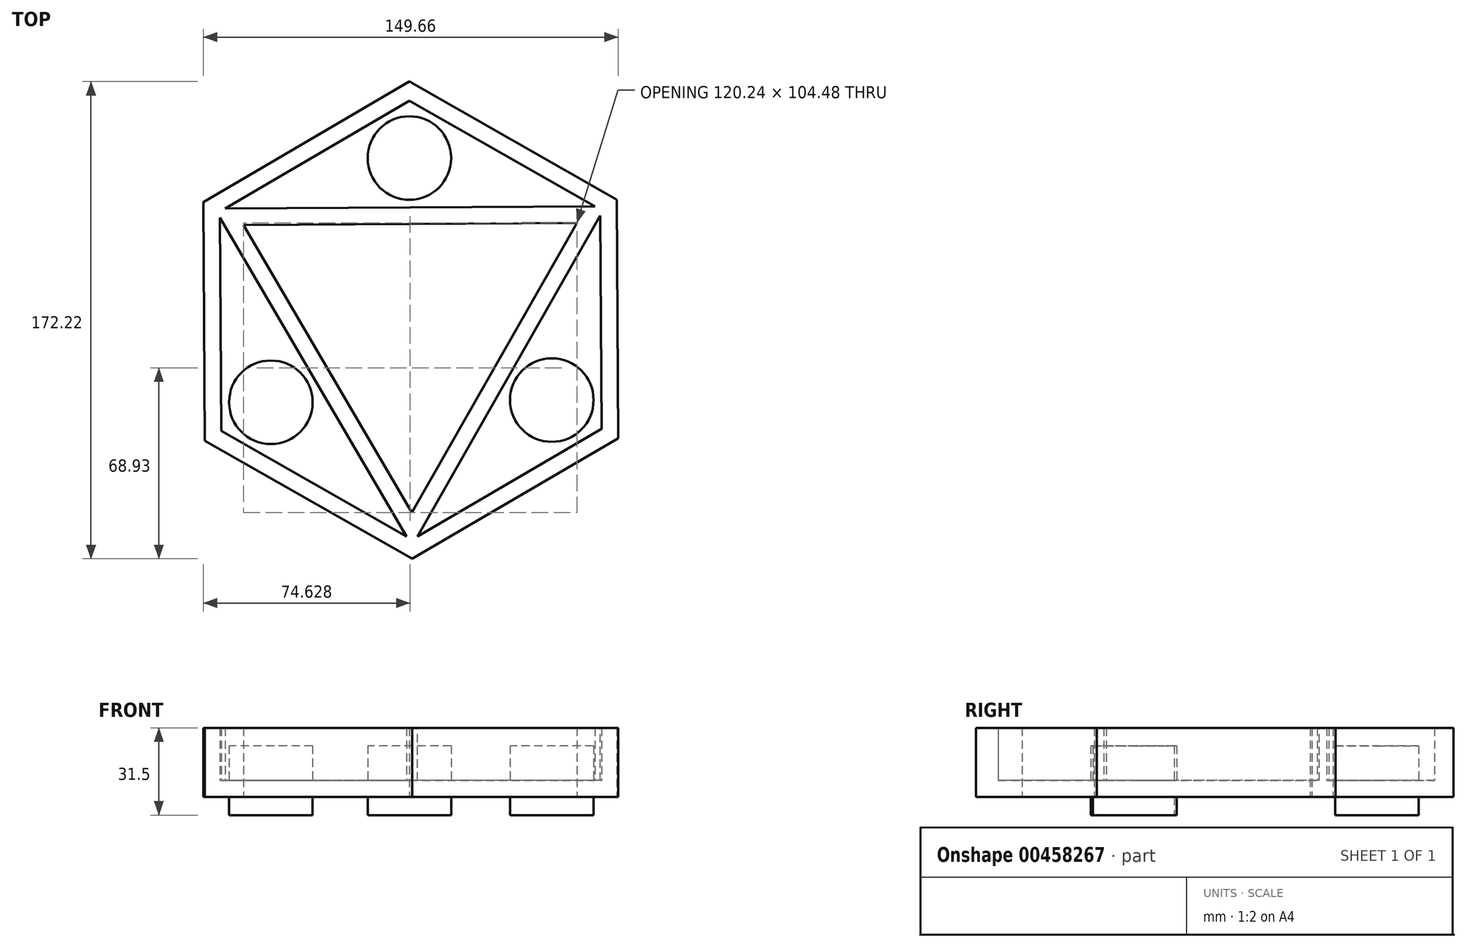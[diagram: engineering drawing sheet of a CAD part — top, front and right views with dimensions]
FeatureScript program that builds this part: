
annotation { "Feature Type Name" : "Feature", "Feature Type Description" : "" }
export const myFeature = defineFeature(function(context is Context, id is Id, definition is map)
    precondition{}
    {
        {
            var Q0;
            Q0=qCreatedBy(makeId("Top.planeOp"),FACE);
            var sketch = newSketch(context, id + "F0", { "sketchPlane" : qUnion([Q0])});
            skLineSegment(sketch, "E0.0", {"start": v(-0.5, 86.11) * mm, "end": v(74.32, 43.5) * mm});
            skLineSegment(sketch, "E0.1", {"start": v(74.32, 43.5) * mm, "end": v(74.83, -42.62) * mm});
            skLineSegment(sketch, "E0.2", {"start": v(74.83, -42.62) * mm, "end": v(0.5, -86.11) * mm});
            skLineSegment(sketch, "E0.3", {"start": v(0.5, -86.11) * mm, "end": v(-74.32, -43.5) * mm});
            skLineSegment(sketch, "E0.4", {"start": v(-74.32, -43.5) * mm, "end": v(-74.83, 42.62) * mm});
            skLineSegment(sketch, "E0.5", {"start": v(-74.83, 42.62) * mm, "end": v(-0.5, 86.11) * mm});
            skPoint(sketch, "E0.0.midPoint", {"position": v(36.91, 64.8) * mm});
            skPoint(sketch, "E1.center", {"position": v(0, 0) * mm});
            skPoint(sketch, "E2.orphan", {"position": v(0.5, -86.11) * mm});
            skPoint(sketch, "E3.orphan", {"position": v(74.32, 43.5) * mm});
            skLineSegment(sketch, "E4", {"start": v(-30.16, 17.18) * mm, "end": v(29.96, 17.53) * mm});
            skLineSegment(sketch, "E5", {"start": v(0.2, -34.7) * mm, "end": v(29.96, 17.53) * mm});
            skLineSegment(sketch, "E6", {"start": v(-30.16, 17.18) * mm, "end": v(0.2, -34.7) * mm});
            skPoint(sketch, "E1.2.0.start.orphan", {"position": v(0, 0) * mm});
            skPoint(sketch, "E1.1.0.start.orphan", {"position": v(0, 0) * mm});
            skPoint(sketch, "E7.end.orphan", {"position": v(0.4, -69.42) * mm});
            skPoint(sketch, "E8.end.orphan", {"position": v(-60.32, 34.36) * mm});
            skPoint(sketch, "E9.end.orphan", {"position": v(59.92, 35.06) * mm});
            skLineSegment(sketch, "E10", {"start": v(-60.32, 34.36) * mm, "end": v(0.4, -69.42) * mm});
            skLineSegment(sketch, "E11", {"start": v(59.92, 35.06) * mm, "end": v(0.4, -69.42) * mm});
            skLineSegment(sketch, "E12", {"start": v(59.92, 35.06) * mm, "end": v(-60.32, 34.36) * mm});
            skSolve(sketch);
        }
        {
            var Q0;
            Q0=makeQuery(id+"F0.imprint","IMPRINT",FACE,{"disambiguationData":[TD([[makeQuery(id+"F0.imprint","IMPRINT",EDGE,{"derivedFrom":sQuery(id+"F0.wireOp",EDGE,"E0.0")}),-1.0]])]});
            var Q1;
            Q1=makeQuery(id+"F0.imprint","IMPRINT",FACE,{"disambiguationData":[TD([[makeQuery(id+"F0.imprint","IMPRINT",EDGE,{"derivedFrom":sQuery(id+"F0.wireOp",EDGE,"E4")}),-1.0]])]});
            extrude(context, id + "F1", {"entities" : qUnion([Q0, Q1]), "depth" : 25 * mm});
        }
        {
            var Q0;
            Q0=makeQuery(id+"F1.opExtrude","CAP_FACE",FACE,{"disambiguationData":[OSD([sQuery(id+"F0.wireOp",EDGE,"E0.0"),sQuery(id+"F0.wireOp",EDGE,"E0.1"),sQuery(id+"F0.wireOp",EDGE,"E0.2"),sQuery(id+"F0.wireOp",EDGE,"E0.3"),sQuery(id+"F0.wireOp",EDGE,"E0.4"),sQuery(id+"F0.wireOp",EDGE,"E0.5"),sQuery(id+"F0.wireOp",EDGE,"E10"),sQuery(id+"F0.wireOp",EDGE,"E11"),sQuery(id+"F0.wireOp",EDGE,"E12")])],"isStart":false});
            shell(context, id + "F2", {"entities" : qUnion([Q0]), "thickness" : 6 * mm});
        }
        {
            var Q0;
            Q0=makeQuery(id+"F1.opExtrude","SWEPT_BODY",BODY,{"disambiguationData":[OSD([sQuery(id+"F0.wireOp",EDGE,"E4"),sQuery(id+"F0.wireOp",EDGE,"E5"),sQuery(id+"F0.wireOp",EDGE,"E6")])]});
            deleteBodies(context, id + "F3", {"entities" : qUnion([Q0])});
        }
        {
            var Q0;
            Q0=makeQuery(id+"F2.opShell","OFFSET_FACE",FACE,{"disambiguationData":[OSD([sQuery(id+"F0.wireOp",EDGE,"E0.0"),sQuery(id+"F0.wireOp",EDGE,"E0.1"),sQuery(id+"F0.wireOp",EDGE,"E0.2"),sQuery(id+"F0.wireOp",EDGE,"E0.3"),sQuery(id+"F0.wireOp",EDGE,"E0.4"),sQuery(id+"F0.wireOp",EDGE,"E0.5"),sQuery(id+"F0.wireOp",EDGE,"E10"),sQuery(id+"F0.wireOp",EDGE,"E11"),sQuery(id+"F0.wireOp",EDGE,"E12")]),OD(0.0)]});
            var sketch = newSketch(context, id + "F4", { "sketchPlane" : qUnion([Q0])});
            skCircle(sketch, "E13", {"center": v(-0.46, 58.5) * mm, "radius": 15.06 * mm});
            skCircle(sketch, "E14.1.0", {"center": v(-50.42, -29.65) * mm, "radius": 15.06 * mm});
            skCircle(sketch, "E14.2.0", {"center": v(50.88, -28.85) * mm, "radius": 15.06 * mm});
            skPoint(sketch, "E14.center", {"position": v(0, 0) * mm});
            skSolve(sketch);
        }
        {
            var Q0;
            Q0=makeQuery(id+"F4.imprint","IMPRINT",FACE,{"disambiguationData":[TD([[makeQuery(id+"F4.imprint","IMPRINT",EDGE,{"derivedFrom":sQuery(id+"F4.wireOp",EDGE,"E13")}),1.0]])]});
            var Q1;
            Q1=makeQuery(id+"F4.imprint","IMPRINT",FACE,{"disambiguationData":[TD([[makeQuery(id+"F4.imprint","IMPRINT",EDGE,{"derivedFrom":sQuery(id+"F4.wireOp",EDGE,"E14.2.0")}),1.0]])]});
            var Q2;
            Q2=makeQuery(id+"F4.imprint","IMPRINT",FACE,{"disambiguationData":[TD([[makeQuery(id+"F4.imprint","IMPRINT",EDGE,{"derivedFrom":sQuery(id+"F4.wireOp",EDGE,"E14.1.0")}),1.0]])]});
            extrude(context, id + "F5", {"entities" : qUnion([Q0, Q1, Q2]), "operationType" : NewBodyOperationType.ADD, "depth" : 25 * mm, "symmetric" : true});
        }
    });
